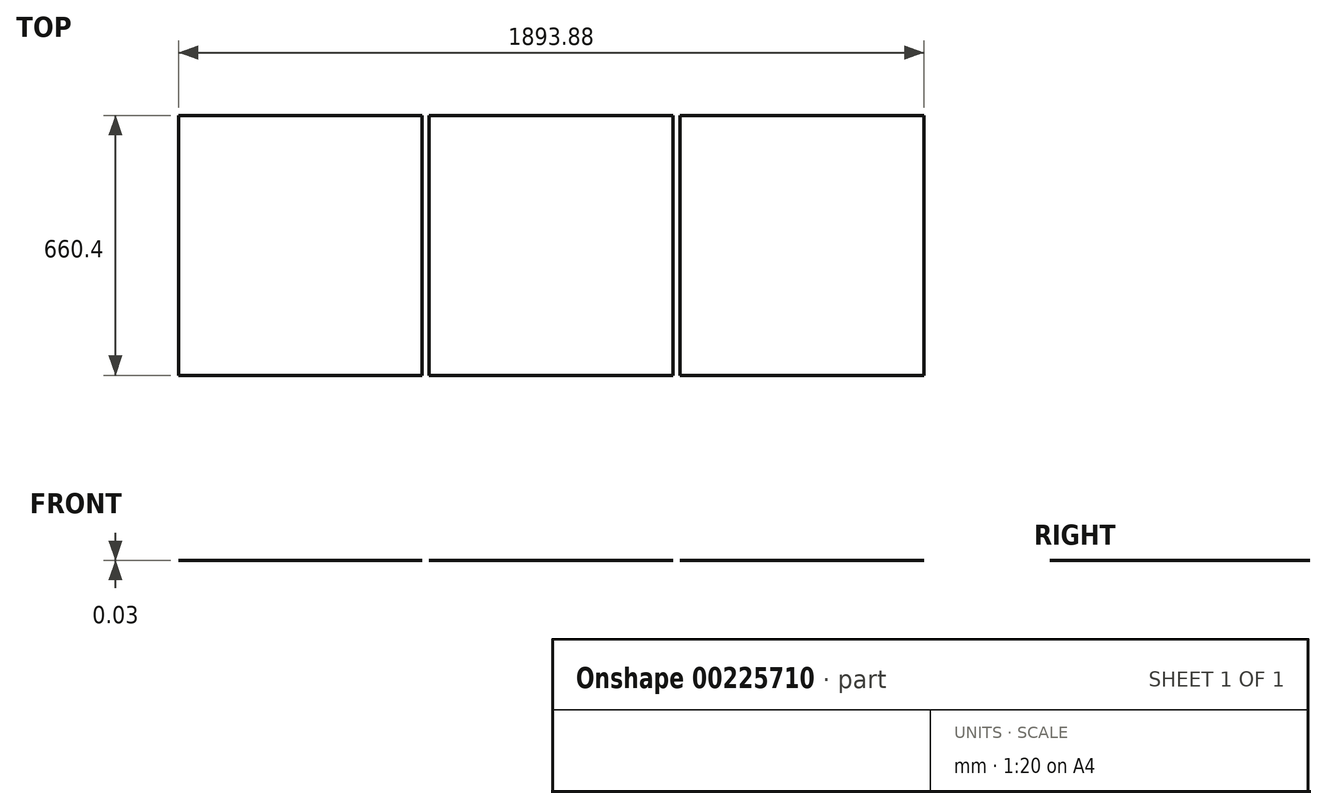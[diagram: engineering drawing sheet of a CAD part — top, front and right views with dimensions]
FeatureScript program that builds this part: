
annotation { "Feature Type Name" : "Feature", "Feature Type Description" : "" }
export const myFeature = defineFeature(function(context is Context, id is Id, definition is map)
    precondition{}
    {
        {
            var Q0;
            Q0=qCreatedBy(makeId("Top.planeOp"),FACE);
            var sketch = newSketch(context, id + "F0", { "sketchPlane" : qUnion([Q0])});
            skLineSegment(sketch, "E0.bottom", {"start": v(-662.7, 325) * mm, "end": v(1267.7, 325) * mm});
            skLineSegment(sketch, "E0.top", {"start": v(-662.7, -335.4) * mm, "end": v(1267.7, -335.4) * mm});
            skLineSegment(sketch, "E0.left", {"start": v(-662.7, 325) * mm, "end": v(-662.7, -335.4) * mm});
            skLineSegment(sketch, "E0.right", {"start": v(1267.7, 325) * mm, "end": v(1267.7, -335.4) * mm});
            skSolve(sketch);
        }
        {
            var Q0;
            Q0 = qSketchRegion(id + "F0", true);
            extrude(context, id + "F1", {"entities" : qUnion([Q0]), "oppositeDirection" : true, "depth" : 23 / 812.8 * mm});
        }
        {
            var Q0;
            Q0=makeQuery(id+"F1.opExtrude","SWEPT_FACE",FACE,{"disambiguationData":[OSD([sQuery(id+"F0.wireOp",EDGE,"E0.top")])]});
            var sketch = newSketch(context, id + "F2", { "sketchPlane" : qUnion([Q0])});
            skLineSegment(sketch, "E1.bottom", {"start": v(-662.7, 0) * mm, "end": v(-644.45, 0) * mm});
            skLineSegment(sketch, "E1.top", {"start": v(-662.7, -6.35) * mm, "end": v(-644.45, -6.35) * mm});
            skLineSegment(sketch, "E1.left", {"start": v(-662.7, 0) * mm, "end": v(-662.7, -6.35) * mm});
            skLineSegment(sketch, "E1.right", {"start": v(-644.45, 0) * mm, "end": v(-644.45, -6.35) * mm});
            skSolve(sketch);
        }
        {
            var Q0;
            Q0=makeQuery(id+"F2.imprint","IMPRINT",FACE,{"disambiguationData":[TD([[makeQuery(id+"F2.imprint","IMPRINT",EDGE,{"derivedFrom":sQuery(id+"F2.wireOp",EDGE,"E1.bottom")}),-1.0]])]});
            extrude(context, id + "F3", {"entities" : qUnion([Q0]), "operationType" : NewBodyOperationType.REMOVE, "endBound" : BoundingType.THROUGH_ALL, "oppositeDirection" : true, "depth" : 25.4 * mm});
        }
        {
            var Q0;
            Q0=makeQuery(id+"F1.opExtrude","SWEPT_FACE",FACE,{"disambiguationData":[OSD([sQuery(id+"F0.wireOp",EDGE,"E0.top")])]});
            var sketch = newSketch(context, id + "F4", { "sketchPlane" : qUnion([Q0])});
            skLineSegment(sketch, "E2.bottom", {"start": v(1267.7, 0) * mm, "end": v(1249.43, 0) * mm});
            skLineSegment(sketch, "E2.top", {"start": v(1267.7, -6.35) * mm, "end": v(1249.43, -6.35) * mm});
            skLineSegment(sketch, "E2.left", {"start": v(1267.7, 0) * mm, "end": v(1267.7, -6.35) * mm});
            skLineSegment(sketch, "E2.right", {"start": v(1249.43, 0) * mm, "end": v(1249.43, -6.35) * mm});
            skSolve(sketch);
        }
        {
            var Q0;
            Q0=makeQuery(id+"F4.imprint","IMPRINT",FACE,{"disambiguationData":[TD([[makeQuery(id+"F4.imprint","IMPRINT",EDGE,{"derivedFrom":sQuery(id+"F4.wireOp",EDGE,"E2.bottom")}),-1.0]])]});
            extrude(context, id + "F5", {"entities" : qUnion([Q0]), "operationType" : NewBodyOperationType.REMOVE, "endBound" : BoundingType.THROUGH_ALL, "oppositeDirection" : true, "depth" : 25.4 * mm});
        }
        {
            var Q0;
            Q0=makeQuery(id+"F1.opExtrude","SWEPT_FACE",FACE,{"disambiguationData":[OSD([sQuery(id+"F0.wireOp",EDGE,"E0.top")])]});
            var sketch = newSketch(context, id + "F6", { "sketchPlane" : qUnion([Q0])});
            skLineSegment(sketch, "E3.bottom", {"start": v(612.05, 0) * mm, "end": v(630.3, 0) * mm});
            skLineSegment(sketch, "E3.top", {"start": v(612.05, -6.35) * mm, "end": v(630.3, -6.35) * mm});
            skLineSegment(sketch, "E3.left", {"start": v(612.05, 0) * mm, "end": v(612.05, -6.35) * mm});
            skLineSegment(sketch, "E3.right", {"start": v(630.3, 0) * mm, "end": v(630.3, -6.35) * mm});
            skSolve(sketch);
        }
        {
            var Q0;
            Q0=makeQuery(id+"F6.imprint","IMPRINT",FACE,{"disambiguationData":[TD([[makeQuery(id+"F6.imprint","IMPRINT",EDGE,{"derivedFrom":sQuery(id+"F6.wireOp",EDGE,"E3.bottom")}),-1.0]])]});
            extrude(context, id + "F7", {"entities" : qUnion([Q0]), "operationType" : NewBodyOperationType.REMOVE, "endBound" : BoundingType.THROUGH_ALL, "oppositeDirection" : true, "depth" : 25.4 * mm});
        }
        {
            var Q0;
            Q0=makeQuery(id+"F1.opExtrude","SWEPT_FACE",FACE,{"disambiguationData":[OSD([sQuery(id+"F0.wireOp",EDGE,"E0.top")])]});
            var sketch = newSketch(context, id + "F8", { "sketchPlane" : qUnion([Q0])});
            skLineSegment(sketch, "E4.bottom", {"start": v(-25.33, 0) * mm, "end": v(-7.07, 0) * mm});
            skLineSegment(sketch, "E4.top", {"start": v(-25.33, -6.35) * mm, "end": v(-7.07, -6.35) * mm});
            skLineSegment(sketch, "E4.left", {"start": v(-25.33, 0) * mm, "end": v(-25.33, -6.35) * mm});
            skLineSegment(sketch, "E4.right", {"start": v(-7.07, 0) * mm, "end": v(-7.07, -6.35) * mm});
            skSolve(sketch);
        }
        {
            var Q0;
            Q0=makeQuery(id+"F8.imprint","IMPRINT",FACE,{"disambiguationData":[TD([[makeQuery(id+"F8.imprint","IMPRINT",EDGE,{"derivedFrom":sQuery(id+"F8.wireOp",EDGE,"E4.bottom")}),-1.0]])]});
            extrude(context, id + "F9", {"entities" : qUnion([Q0]), "operationType" : NewBodyOperationType.REMOVE, "endBound" : BoundingType.THROUGH_ALL, "oppositeDirection" : true, "depth" : 25.4 * mm});
        }
    });
